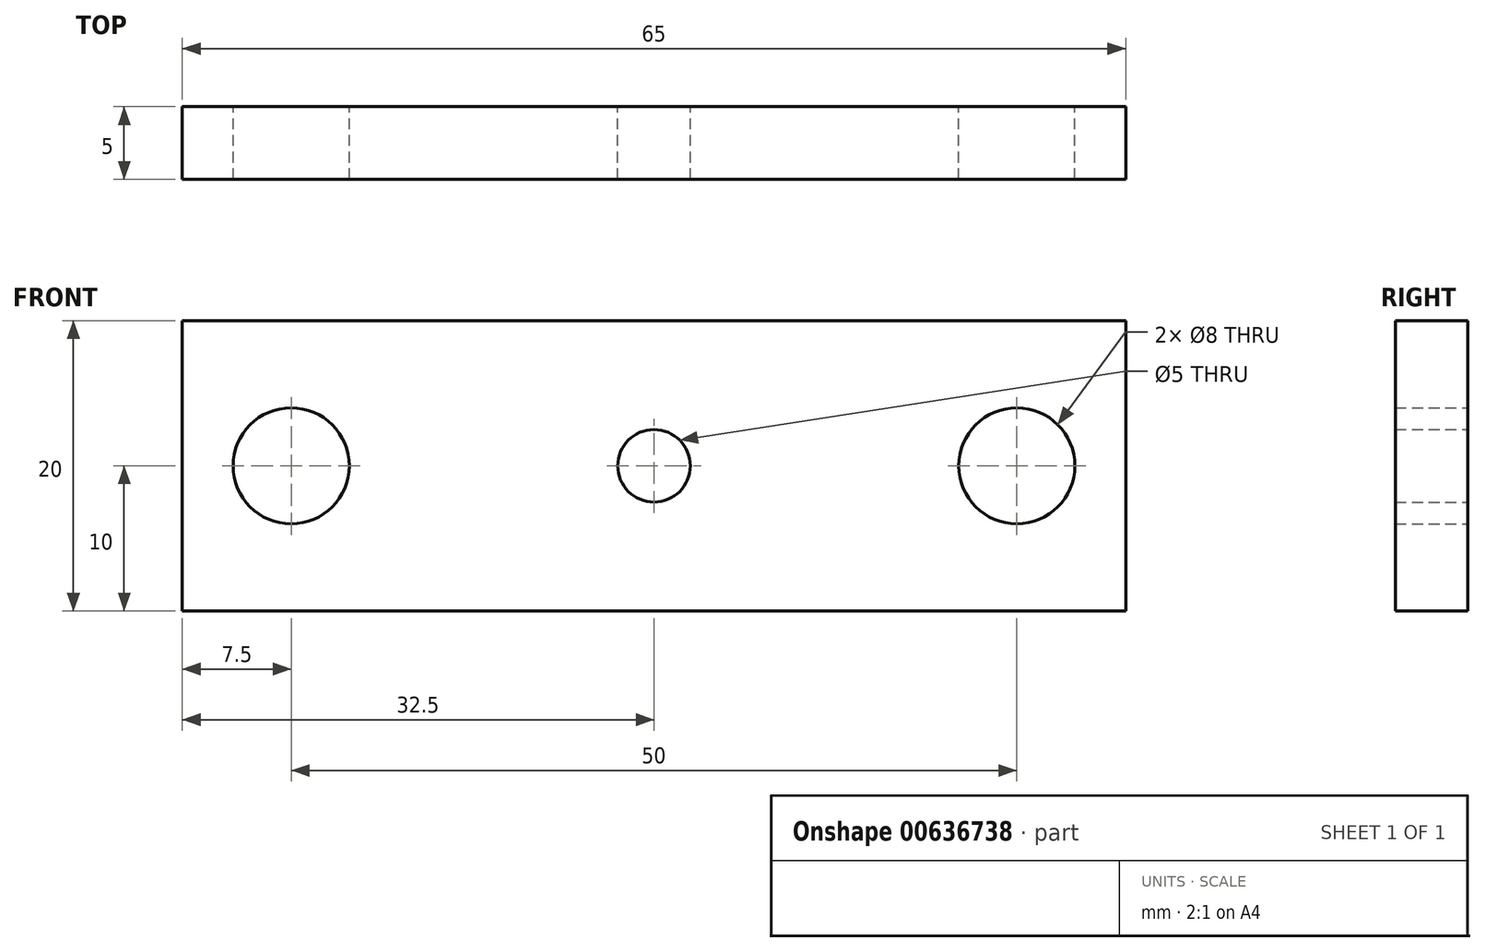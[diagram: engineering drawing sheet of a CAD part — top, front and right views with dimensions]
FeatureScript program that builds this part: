
annotation { "Feature Type Name" : "Feature", "Feature Type Description" : "" }
export const myFeature = defineFeature(function(context is Context, id is Id, definition is map)
    precondition{}
    {
        {
            var Q0;
            Q0=qCreatedBy(makeId("Front.planeOp"),FACE);
            var sketch = newSketch(context, id + "F0", { "sketchPlane" : qUnion([Q0])});
            skLineSegment(sketch, "E0.bottom", {"start": v(-32.5, 10) * mm, "end": v(32.5, 10) * mm});
            skLineSegment(sketch, "E0.top", {"start": v(-32.5, -10) * mm, "end": v(32.5, -10) * mm});
            skLineSegment(sketch, "E0.left", {"start": v(-32.5, 10) * mm, "end": v(-32.5, -10) * mm});
            skLineSegment(sketch, "E0.right", {"start": v(32.5, 10) * mm, "end": v(32.5, -10) * mm});
            skPoint(sketch, "E0.middle", {"position": v(0, 0) * mm});
            skCircle(sketch, "E1", {"center": v(0, 0) * mm, "radius": 2.5 * mm});
            skLineSegment(sketch, "E2", {"start": v(0, 0) * mm, "end": v(-25, 0) * mm, "construction": true});
            skLineSegment(sketch, "E3", {"start": v(0, 0) * mm, "end": v(25, 0) * mm, "construction": true});
            skCircle(sketch, "E4", {"center": v(-25, 0) * mm, "radius": 4 * mm});
            skCircle(sketch, "E5", {"center": v(25, 0) * mm, "radius": 4 * mm});
            skSolve(sketch);
        }
        {
            var Q0;
            Q0=makeQuery(id+"F0.imprint","IMPRINT",FACE,{"disambiguationData":[TD([[makeQuery(id+"F0.imprint","IMPRINT",EDGE,{"derivedFrom":sQuery(id+"F0.wireOp",EDGE,"E0.bottom")}),-1.0]])]});
            extrude(context, id + "F1", {"entities" : qUnion([Q0]), "depth" : 5 * mm, "offsetDistance" : 25 * mm});
        }
    });
